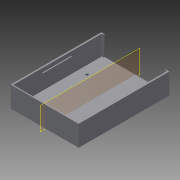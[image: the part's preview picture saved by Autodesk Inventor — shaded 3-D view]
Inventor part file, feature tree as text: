
AUTODESK INVENTOR PART (.ipt)
format: ipt  version: 2015 SP2 (Build 190223200, 223)  size: 173,056 bytes
history: native  units: in
note: dims shown in document units (in); Inventor stores cm internally (conversion verified against a paired STEP export)
features: sketch x8, extrude x6, projected_geometry x3, hole x1, plane x1, mirror x1
ambient origin geometry x8: Origin, YZ Plane, XZ Plane, XY Plane, X Axis, Y Axis, Z Axis, Center Point
bodies: Solid1 (feature_tree)
feature tree (20):
  extrude  "Extrusion1"  Depth=3.3465in
  sketch  "Sketch2"  dims[d2=0.1969in d3=0.0394in d4=0.0in]
  hole  "Hole1"  [1 undecoded]
  extrude  "Extrusion4"  Depth=3.3465in
  extrude  "Extrusion5"  Depth=0.1083in
  extrude  "Extrusion6"  Depth=0.1083in
  extrude  "Extrusion7"  Depth=2.2835in
  sketch  "Sketch8"  dims[d22=2.2835in d23=1.9291in]
  extrude  "Extrusion8"  Depth=1.9291in
  plane  "Work Plane2"
  mirror  "Mirror1"
  sketch  "Sketch1"  dims[d0=2.2047in d1=3.3465in]
  projected_geometry  "Projected Loop1"
  sketch  "Sketch4"  dims[d14=2.2047in d15=3.3465in]
  sketch  "Sketch5"  dims[d16=0.1083in d17=0.1083in]
  sketch  "Sketch6"  dims[d18=0.1083in d19=0.1083in]
  projected_geometry  "Projected Loop2"
  sketch  "Sketch7"  dims[d20=1.9291in d21=2.2835in]
  projected_geometry  "Projected Loop3"
  sketch  "Sketch9"  dims[d24=0.2441in d25=0.2441in d26=0.2441in d27=0.2441in d28=0.1378in d29=0.1378in d30=0.1378in d31=0.1378in d32=0.1378in d33=0.1083in d34=0.2362in d35=0.1575in d36=0.0787in d37=90.0deg d38=0.315in d39=0.8108in d41=0.0394in d42=0.7874in d43=0.0394in d44=0.0in d45=0.0in d46=0.0787in d47=0.0787in d48=0.0787in d49=0.0in d50=3.5433in d51=0.0197in d52=0.0in d53=0.0197in d54=0.0in d55=3.622in d56=2.7165in d59=0.0394in d60=0.0in d61=-1.3583in d62=0.1575in d63=0.0394in d64=1.1811in d65=1.1811in d66=1.1811in]
note: 1 required parameter value undecoded (feature->parameter linkage not recoverable at this tier; creation-order binding heuristic only, values carry confidence <= 0.55)
